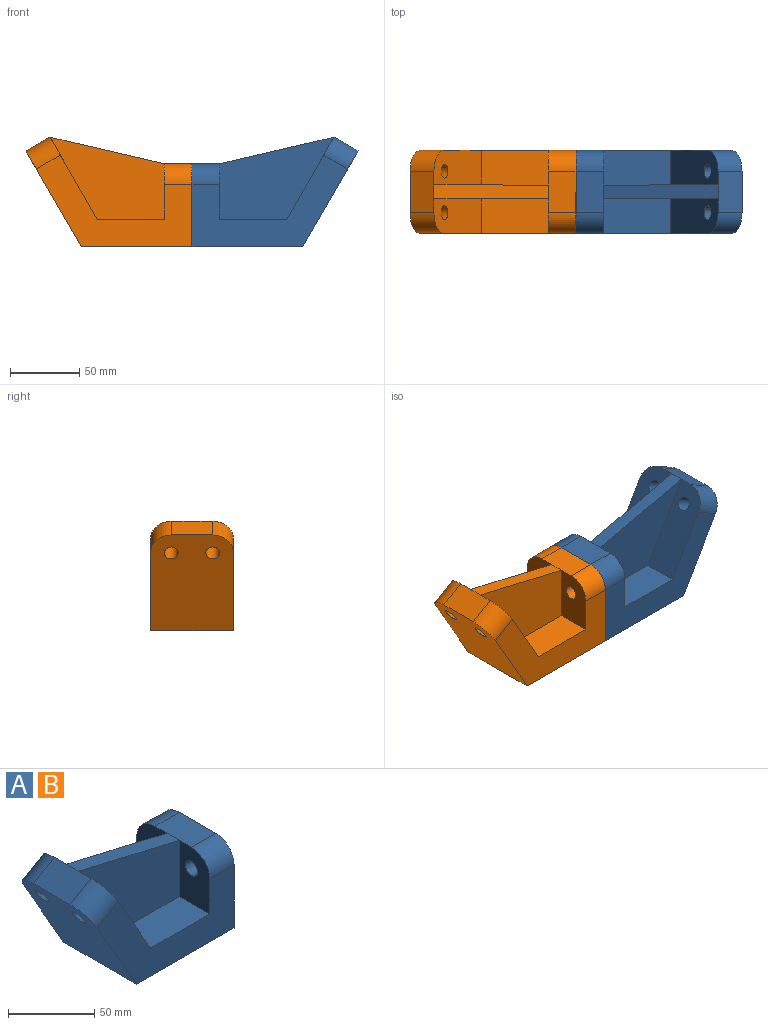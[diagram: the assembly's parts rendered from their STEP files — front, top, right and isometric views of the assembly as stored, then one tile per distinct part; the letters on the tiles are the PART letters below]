
ASSEMBLY  parts=2 mates=1
PART A: 24 faces, bbox 120x60x79.3 mm
  f0: plane 69.28x60mm, normal (-0.87,0,-0.5), area 4546.3mm2, adj f6,f9,f10,f11,f18,f19,f22,f23
  f1: plane 60x60mm, normal (1,0,0), area 3346.3mm2, adj f6,f7,f9,f10,f16,f17,f20,f21
  f2: plane 48.45x25mm, normal (0,0,1), area 1211.3mm2, adj f3,f4,f10,f14
  f3: plane 40x25mm, normal (-1,0,0), area 873.2mm2, adj f2,f7,f10,f14,f16,f21
  f4: plane 59.28x34.23mm, normal (0.87,0,0.5), area 1584.5mm2, adj f2,f10,f11,f14,f19,f23
  f5: plane 48.45x25mm, normal (0,0,1), area 1211.3mm2, adj f8,f9,f12,f13
  f6: plane 80x60mm, normal (0,0,-1), area 4800mm2, adj f0,f1,f9,f10
  f7: plane 30x20mm, normal (0,0,1), area 600mm2, adj f1,f3,f8,f15,f16,f17
  f8: plane 40x25mm, normal (-1,0,0), area 873.2mm2, adj f5,f7,f9,f13,f17,f20
  f9: plane 112.5x66.29mm, normal (0,-1,0), area 3169.1mm2, adj f0,f1,f5,f6,f8,f12,f17,f18
  f10: plane 112.5x66.29mm, normal (0,1,0), area 3169.1mm2, adj f0,f1,f2,f3,f4,f6,f16,f19
  f11: plane 30x17.32mm, normal (-0.5,0,0.87), area 600mm2, adj f0,f4,f12,f15,f18,f19
  f12: plane 59.28x34.23mm, normal (0.87,0,0.5), area 1584.5mm2, adj f5,f9,f11,f13,f18,f22
  f13: plane 82.68x59.28mm, normal (0,-1,0), area 3089.8mm2, adj f5,f8,f12,f15
  f14: plane 82.68x59.28mm, normal (0,1,0), area 3089.8mm2, adj f2,f3,f4,f15
  f15: plane 82.68x19.28mm, normal (0.23,0,0.97), area 849mm2, adj f7,f11,f13,f14
  f16: cylinder r=15mm len=20mm, axis (-1,0,0), area 471.2mm2, adj f1,f3,f7,f10
  f17: cylinder r=15mm len=20mm, axis (1,0,0), area 471.2mm2, adj f1,f7,f8,f9
  f18: cylinder r=15mm len=24.82mm, axis (0.87,0,0.5), area 471.2mm2, adj f0,f9,f11,f12
  f19: cylinder r=15mm len=24.82mm, axis (-0.87,0,-0.5), area 471.2mm2, adj f0,f4,f10,f11
  f20: cylinder r=5mm len=20mm, axis (1,0,0), area 628.3mm2, adj f1,f8
  f21: cylinder r=5mm len=20mm, axis (1,0,0), area 628.3mm2, adj f1,f3
  f22: cylinder r=5mm len=22.32mm, axis (-0.87,0,-0.5), area 628.3mm2, adj f0,f12
  f23: cylinder r=5mm len=22.32mm, axis (-0.87,0,-0.5), area 628.3mm2, adj f0,f4
PART B: same geometry as A
PLACE A rot(axis=(0,0,1),180deg) t=(225.68,-155.13,-3.26)mm
PLACE B t=(65.68,-155.13,-3.26)mm
MATE fastened B.f17 <-> A.f16  axis (1,0,0) through (145.68,-170.13,41.74)mm
